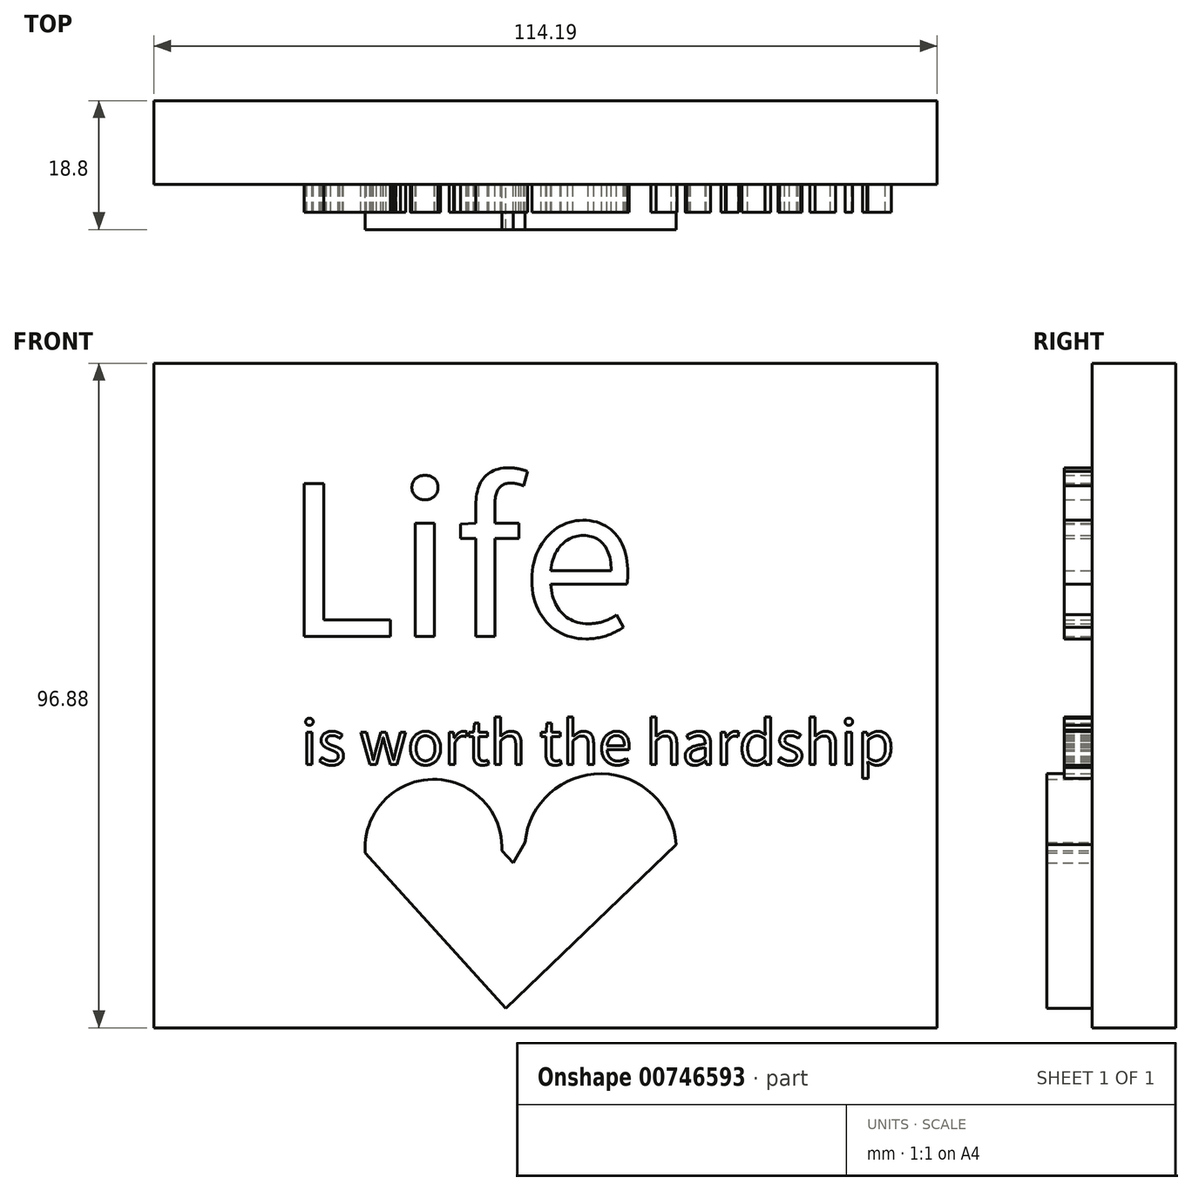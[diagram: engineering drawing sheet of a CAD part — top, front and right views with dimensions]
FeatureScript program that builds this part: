
annotation { "Feature Type Name" : "Feature", "Feature Type Description" : "" }
export const myFeature = defineFeature(function(context is Context, id is Id, definition is map)
    precondition{}
    {
        {
            var Q0;
            Q0=qCreatedBy(makeId("Front.planeOp"),FACE);
            var sketch = newSketch(context, id + "F0", { "sketchPlane" : qUnion([Q0])});
            skLineSegment(sketch, "E0.bottom", {"start": v(-47.97, 39.8) * mm, "end": v(66.22, 39.8) * mm});
            skLineSegment(sketch, "E0.top", {"start": v(-47.97, -57.1) * mm, "end": v(66.22, -57.1) * mm});
            skLineSegment(sketch, "E0.left", {"start": v(-47.97, 39.8) * mm, "end": v(-47.97, -57.1) * mm});
            skLineSegment(sketch, "E0.right", {"start": v(66.22, 39.8) * mm, "end": v(66.22, -57.1) * mm});
            skSolve(sketch);
        }
        {
            var Q0;
            Q0 = qSketchRegion(id + "F0", true);
            extrude(context, id + "F1", {"entities" : qUnion([Q0]), "depth" : 12.2 * mm, "offsetDistance" : 25.4 * mm});
        }
        {
            var Q0;
            Q0=makeQuery(id+"F1.opExtrude","CAP_FACE",FACE,{"disambiguationData":[OSD([sQuery(id+"F0.wireOp",EDGE,"E0.bottom"),sQuery(id+"F0.wireOp",EDGE,"E0.top"),sQuery(id+"F0.wireOp",EDGE,"E0.left"),sQuery(id+"F0.wireOp",EDGE,"E0.right")])],"isStart":false});
            var sketch = newSketch(context, id + "F2", { "sketchPlane" : qUnion([Q0])});
            skText(sketch, "E1", { "text": "Life \n", "fontName": "NotoSansCJKkr-Regular.otf"});
            const initialGuessF2  = {"E1": [-0.0291, 0, 1, 0, 0.02186]};
            skSetInitialGuess(sketch, initialGuessF2);
            skSolve(sketch);
        }
        {
            var Q0;
            Q0 = qSketchRegion(id + "F2", true);
            extrude(context, id + "F3", {"entities" : qUnion([Q0]), "operationType" : NewBodyOperationType.ADD, "depth" : 4.06 * mm, "offsetDistance" : 25.4 * mm});
        }
        {
            var Q0;
            {var subQ0=sQuery(id+"F0.wireOp",EDGE,"E0.top");var subQ1=sQuery(id+"F0.wireOp",EDGE,"E0.right");var subQ2=sQuery(id+"F0.wireOp",EDGE,"E0.bottom");var subQ3=sQuery(id+"F0.wireOp",EDGE,"E0.left");Q0=makeQuery(id+"F3.boolean.opBoolean","SPLIT",FACE,{"disambiguationData":[TD([makeQuery(id+"F1.opExtrude","SWEPT_FACE",FACE,{"disambiguationData":[OSD([subQ2])]})])],"derivedFrom":makeQuery(id+"F1.opExtrude","CAP_FACE",FACE,{"disambiguationData":[OSD([subQ2,subQ0,subQ3,subQ1])],"isStart":false})});}
            var sketch = newSketch(context, id + "F4", { "sketchPlane" : qUnion([Q0])});
            skText(sketch, "E2", { "text": " is worth the hardship", "fontName": "NotoSansCJKkr-Regular.otf"});
            const initialGuessF4  = {"E2": [-0.02847, -0.01872, 1, 0, 0.0063]};
            skSetInitialGuess(sketch, initialGuessF4);
            skSolve(sketch);
        }
        {
            var Q0;
            Q0 = qSketchRegion(id + "F4", true);
            extrude(context, id + "F5", {"entities" : qUnion([Q0]), "operationType" : NewBodyOperationType.ADD, "depth" : 4.06 * mm, "offsetDistance" : 25.4 * mm});
        }
        {
            var Q0;
            {var subQ34=sQuery(id+"F0.wireOp",EDGE,"E0.bottom");var subQ35=makeQuery(id+"F1.opExtrude","SWEPT_FACE",FACE,{"disambiguationData":[OSD([subQ34])]});var subQ40=sQuery(id+"F0.wireOp",EDGE,"E0.left");var subQ43=sQuery(id+"F0.wireOp",EDGE,"E0.right");var subQ45=sQuery(id+"F0.wireOp",EDGE,"E0.top");Q0=makeQuery(id+"F5.boolean.opBoolean","SPLIT",FACE,{"disambiguationData":[TD([subQ35])],"derivedFrom":makeQuery(id+"F3.boolean.opBoolean","SPLIT",FACE,{"disambiguationData":[TD([subQ35])],"derivedFrom":makeQuery(id+"F1.opExtrude","CAP_FACE",FACE,{"disambiguationData":[OSD([subQ34,subQ45,subQ40,subQ43])],"isStart":false})})});}
            var sketch = newSketch(context, id + "F6", { "sketchPlane" : qUnion([Q0])});
            skLineSegment(sketch, "E3", {"start": v(-17.14, -31.61) * mm, "end": v(3.3, -54.26) * mm});
            skLineSegment(sketch, "E4", {"start": v(3.3, -54.26) * mm, "end": v(28.15, -30.36) * mm});
            skArc(sketch, "E5", {"start": v(2.75, -31.3) * mm, "mid": v(-7.36, -20.87) * mm, "end": v(-17.14, -31.61) * mm});
            skArc(sketch, "E6", {"start": v(28.15, -30.36) * mm, "mid": v(17.29, -20.05) * mm, "end": v(6.13, -30.04) * mm});
            skLineSegment(sketch, "E7", {"start": v(2.75, -31.3) * mm, "end": v(4.43, -33.04) * mm});
            skLineSegment(sketch, "E8", {"start": v(4.43, -33.04) * mm, "end": v(6.13, -30.04) * mm});
            skSolve(sketch);
        }
        {
            var Q0;
            Q0 = qSketchRegion(id + "F6", true);
            extrude(context, id + "F7", {"entities" : qUnion([Q0]), "operationType" : NewBodyOperationType.ADD, "depth" : 6.6 * mm, "offsetDistance" : 25.4 * mm});
        }
    });
